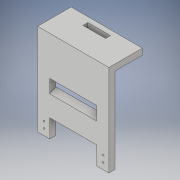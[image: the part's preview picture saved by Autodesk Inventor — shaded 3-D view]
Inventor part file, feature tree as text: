
AUTODESK INVENTOR PART (.ipt)
format: ipt  version: 2019 (Build 230136000, 136)  size: 187,392 bytes
history: native  units: in
note: dims shown in document units (in); Inventor stores cm internally (conversion verified against a paired STEP export)
features: sketch x8, extrude x6, other x1, mirror x1, loft x1, projected_geometry x1
ambient origin geometry x8: Origin, YZ Plane, XZ Plane, XY Plane, X Axis, Y Axis, Z Axis, Center Point
bodies: Body1 (feature_tree)
feature tree (18):
  other  "實體1"
  extrude  "擠出1"  Depth=1.1811in
  extrude  "擠出4"  Depth=0.7874in
  mirror  "鏡射1"
  extrude  "擠出5"  Depth=1.437in
  extrude  "擠出6"  Depth=0.1969in TaperAngle=0.0deg
  extrude  "擠出7"  Depth=0.1969in
  loft  "斷面混成2"
  extrude  "擠出10"  Depth=4.7244in TaperAngle=0.0deg
  sketch  "草圖1"
  sketch  "草圖4"
  sketch  "草圖5"
  sketch  "草圖6"
  sketch  "草圖7"
  projected_geometry  "投影迴路1"
  sketch  "草圖11"
  sketch  "草圖12"
  sketch  "草圖13"
